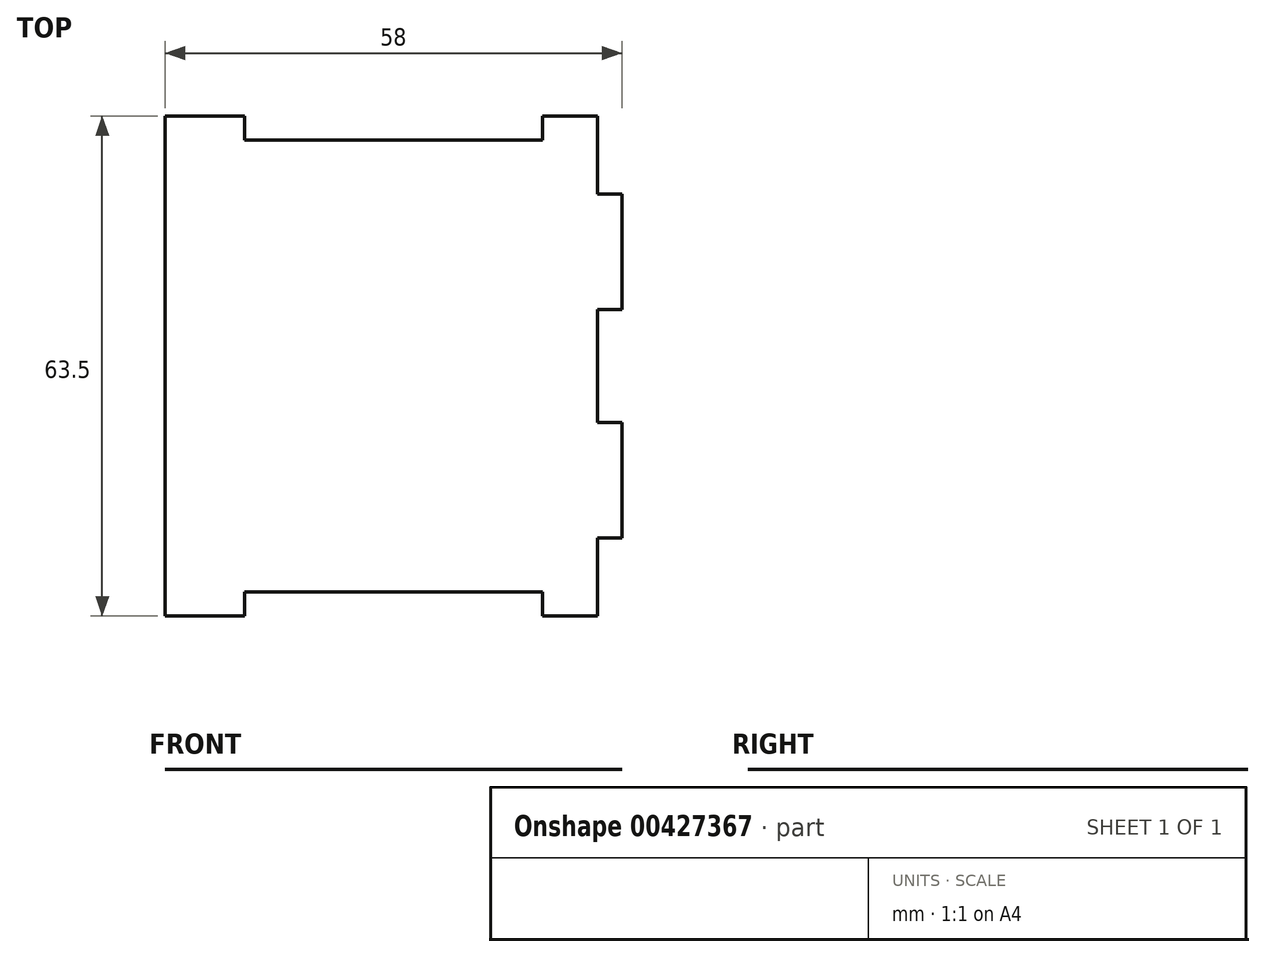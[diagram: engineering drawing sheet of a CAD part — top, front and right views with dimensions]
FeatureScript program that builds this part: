
annotation { "Feature Type Name" : "Feature", "Feature Type Description" : "" }
export const myFeature = defineFeature(function(context is Context, id is Id, definition is map)
    precondition{}
    {
        {
            var Q0;
            Q0=qCreatedBy(makeId("Top.planeOp"),FACE);
            var sketch = newSketch(context, id + "F0", { "sketchPlane" : qUnion([Q0])});
            skLineSegment(sketch, "E0.bottom", {"start": v(29, 31.75) * mm, "end": v(-29, 31.75) * mm});
            skLineSegment(sketch, "E0.top", {"start": v(29, -31.75) * mm, "end": v(-29, -31.75) * mm});
            skLineSegment(sketch, "E0.left", {"start": v(29, 31.75) * mm, "end": v(29, -31.75) * mm});
            skLineSegment(sketch, "E0.right", {"start": v(-29, 31.75) * mm, "end": v(-29, -31.75) * mm});
            skPoint(sketch, "E0.middle", {"position": v(0, 0) * mm});
            skSolve(sketch);
        }
        {
            var Q0;
            Q0=makeQuery(id+"F0.imprint","IMPRINT",FACE,{"disambiguationData":[TD([[makeQuery(id+"F0.imprint","IMPRINT",EDGE,{"derivedFrom":sQuery(id+"F0.wireOp",EDGE,"E0.bottom")}),1.0]])]});
            extrude(context, id + "F1", {"entities" : qUnion([Q0]), "depth" : 1 / 203.2 * mm, "offsetDistance" : 25 * mm});
        }
        {
            var Q0;
            Q0=makeQuery(id+"F1.opExtrude","CAP_FACE",FACE,{"disambiguationData":[OSD([sQuery(id+"F0.wireOp",EDGE,"E0.bottom"),sQuery(id+"F0.wireOp",EDGE,"E0.top"),sQuery(id+"F0.wireOp",EDGE,"E0.left"),sQuery(id+"F0.wireOp",EDGE,"E0.right")])],"isStart":false});
            var sketch = newSketch(context, id + "F2", { "sketchPlane" : qUnion([Q0])});
            skLineSegment(sketch, "E1.bottom", {"start": v(-29, 31.75) * mm, "end": v(29, 31.75) * mm, "construction": true});
            skLineSegment(sketch, "E1.top", {"start": v(-29, -31.75) * mm, "end": v(29, -31.75) * mm, "construction": true});
            skLineSegment(sketch, "E1.left", {"start": v(-29, 31.75) * mm, "end": v(-29, -31.75) * mm, "construction": true});
            skLineSegment(sketch, "E1.right", {"start": v(29, 31.75) * mm, "end": v(29, -31.75) * mm, "construction": true});
            skLineSegment(sketch, "E2", {"start": v(-25.93, 31.75) * mm, "end": v(-25.93, -31.75) * mm, "construction": true});
            skLineSegment(sketch, "E3", {"start": v(25.93, 31.75) * mm, "end": v(25.93, -31.75) * mm, "construction": true});
            skLineSegment(sketch, "E4", {"start": v(-29, -28.68) * mm, "end": v(29, -28.67) * mm, "construction": true});
            skLineSegment(sketch, "E5", {"start": v(-29, 28.67) * mm, "end": v(29, 28.68) * mm, "construction": true});
            skLineSegment(sketch, "E6.0", {"start": v(-19, 31.75) * mm, "end": v(-19, -31.75) * mm, "construction": true});
            skLineSegment(sketch, "E7.0", {"start": v(19, 31.75) * mm, "end": v(19, -31.75) * mm, "construction": true});
            skLineSegment(sketch, "E8.0", {"start": v(-29, -21.75) * mm, "end": v(29, -21.75) * mm, "construction": true});
            skLineSegment(sketch, "E9.0", {"start": v(-29, 21.75) * mm, "end": v(29, 21.75) * mm, "construction": true});
            skLineSegment(sketch, "E10.bottom", {"start": v(18.9, 31.75) * mm, "end": v(-18.9, 31.75) * mm});
            skLineSegment(sketch, "E10.top", {"start": v(18.9, 28.67) * mm, "end": v(-18.9, 28.67) * mm});
            skLineSegment(sketch, "E10.left", {"start": v(18.9, 31.75) * mm, "end": v(18.9, 28.68) * mm});
            skLineSegment(sketch, "E10.right", {"start": v(-18.9, 31.75) * mm, "end": v(-18.9, 28.67) * mm});
            skLineSegment(sketch, "E11.bottom", {"start": v(18.9, -28.67) * mm, "end": v(-18.9, -28.67) * mm});
            skLineSegment(sketch, "E11.top", {"start": v(18.9, -31.75) * mm, "end": v(-18.9, -31.75) * mm});
            skLineSegment(sketch, "E11.left", {"start": v(18.9, -28.67) * mm, "end": v(18.9, -31.75) * mm});
            skLineSegment(sketch, "E11.right", {"start": v(-18.9, -28.68) * mm, "end": v(-18.9, -31.75) * mm});
            skLineSegment(sketch, "E12", {"start": v(25.93, 7.25) * mm, "end": v(29, 7.25) * mm, "construction": true});
            skLineSegment(sketch, "E13", {"start": v(25.93, -7.25) * mm, "end": v(29, -7.25) * mm, "construction": true});
            skLineSegment(sketch, "E14", {"start": v(27.46, -7.25) * mm, "end": v(27.46, -21.75) * mm, "construction": true});
            skLineSegment(sketch, "E15", {"start": v(27.46, -7.25) * mm, "end": v(27.46, 7.25) * mm, "construction": true});
            skLineSegment(sketch, "E16", {"start": v(27.46, 7.25) * mm, "end": v(27.46, 21.75) * mm, "construction": true});
            skLineSegment(sketch, "E17.bottom", {"start": v(29, -7.15) * mm, "end": v(25.93, -7.15) * mm});
            skLineSegment(sketch, "E17.top", {"start": v(29, 7.15) * mm, "end": v(25.93, 7.15) * mm});
            skLineSegment(sketch, "E17.left", {"start": v(29, -7.15) * mm, "end": v(29, 7.15) * mm});
            skLineSegment(sketch, "E17.right", {"start": v(25.93, -7.15) * mm, "end": v(25.93, 7.15) * mm});
            skLineSegment(sketch, "E18.bottom", {"start": v(29, 21.85) * mm, "end": v(25.93, 21.85) * mm});
            skLineSegment(sketch, "E18.top", {"start": v(29, 31.75) * mm, "end": v(25.92, 31.75) * mm});
            skLineSegment(sketch, "E18.left", {"start": v(29, 21.85) * mm, "end": v(29, 31.75) * mm});
            skLineSegment(sketch, "E18.right", {"start": v(25.93, 21.85) * mm, "end": v(25.93, 31.75) * mm});
            skLineSegment(sketch, "E19.bottom", {"start": v(29, -31.75) * mm, "end": v(25.93, -31.75) * mm});
            skLineSegment(sketch, "E19.top", {"start": v(29, -21.85) * mm, "end": v(25.93, -21.85) * mm});
            skLineSegment(sketch, "E19.left", {"start": v(29, -31.75) * mm, "end": v(29, -21.85) * mm});
            skLineSegment(sketch, "E19.right", {"start": v(25.93, -31.75) * mm, "end": v(25.93, -21.85) * mm});
            skSolve(sketch);
        }
        {
            var Q0;
            Q0=makeQuery(id+"F2.imprint","IMPRINT",FACE,{"disambiguationData":[TD([[makeQuery(id+"F2.imprint","IMPRINT",EDGE,{"derivedFrom":sQuery(id+"F2.wireOp",EDGE,"E11.bottom")}),1.0]])]});
            var Q1;
            Q1=makeQuery(id+"F2.imprint","IMPRINT",FACE,{"disambiguationData":[TD([[makeQuery(id+"F2.imprint","IMPRINT",EDGE,{"derivedFrom":sQuery(id+"F2.wireOp",EDGE,"E10.bottom")}),1.0]])]});
            var Q2;
            Q2=makeQuery(id+"F2.imprint","IMPRINT",FACE,{"disambiguationData":[TD([[makeQuery(id+"F2.imprint","IMPRINT",EDGE,{"derivedFrom":sQuery(id+"F2.wireOp",EDGE,"E17.bottom")}),-1.0]])]});
            var Q3;
            Q3=makeQuery(id+"F2.imprint","IMPRINT",FACE,{"disambiguationData":[TD([[makeQuery(id+"F2.imprint","IMPRINT",EDGE,{"derivedFrom":sQuery(id+"F2.wireOp",EDGE,"E19.bottom")}),-1.0]])]});
            var Q4;
            Q4=makeQuery(id+"F2.imprint","IMPRINT",FACE,{"disambiguationData":[TD([[makeQuery(id+"F2.imprint","IMPRINT",EDGE,{"derivedFrom":sQuery(id+"F2.wireOp",EDGE,"E18.bottom")}),-1.0]])]});
            extrude(context, id + "F3", {"entities" : qUnion([Q0, Q1, Q2, Q3, Q4]), "operationType" : NewBodyOperationType.REMOVE, "oppositeDirection" : true, "depth" : 25 * mm, "offsetDistance" : 25 * mm});
        }
    });
